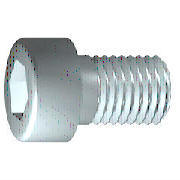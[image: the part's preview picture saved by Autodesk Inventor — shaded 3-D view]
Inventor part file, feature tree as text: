
AUTODESK INVENTOR PART (.ipt)
format: ipt  version: 2021 (Build 250183000, 183)  size: 209,920 bytes
history: native  units: mm (DEFAULTED — no unit token found)
features: sketch x3, extrude x2, plane x1, fillet x1, chamfer x1, projected_geometry x1
ambient origin geometry x7: Origin, YZ Plane, XY Plane, X Axis, Y Axis, Z Axis, Center Point
bodies: Solid1 (feature_tree), Body (feature_tree)
feature tree (9):
  extrude  "Slot"  Depth=3.0mm
  plane  "Work Plane1"
  fillet  "Fillet2"  Radius=3.0mm
  extrude  "Extrusion3"  TaperAngle=60.0deg  [1 undecoded]
  chamfer  "Chamfer3"  Distance=3.0mm
  sketch  "Sketch1"  dims[d1=3.75mm d2=0.306825mm d3=3.0mm]
  sketch  "Sketch2"  dims[d4=1.3mm d5=60.0deg]
  sketch  "Sketch4"  dims[d6=3.0mm d7=3.0mm d8=2.886751mm d9=5.5mm d10=90.0deg d11=10.0mm d12=0.0mm d13=3.75mm d14=0.0mm d15=0.306725mm d16=0.306725mm d17=0.3mm d19=0.0mm d26=5.0mm d27=45.0deg d28=0.0mm d29=0.0mm d30=0.1mm d31=1.0mm d32=0.0mm d33=0.5mm d34=2.0mm d35=45.0deg]
  projected_geometry  "Projected Loop1"
note: 1 required parameter value undecoded (feature->parameter linkage not recoverable at this tier; creation-order binding heuristic only, values carry confidence <= 0.55)
